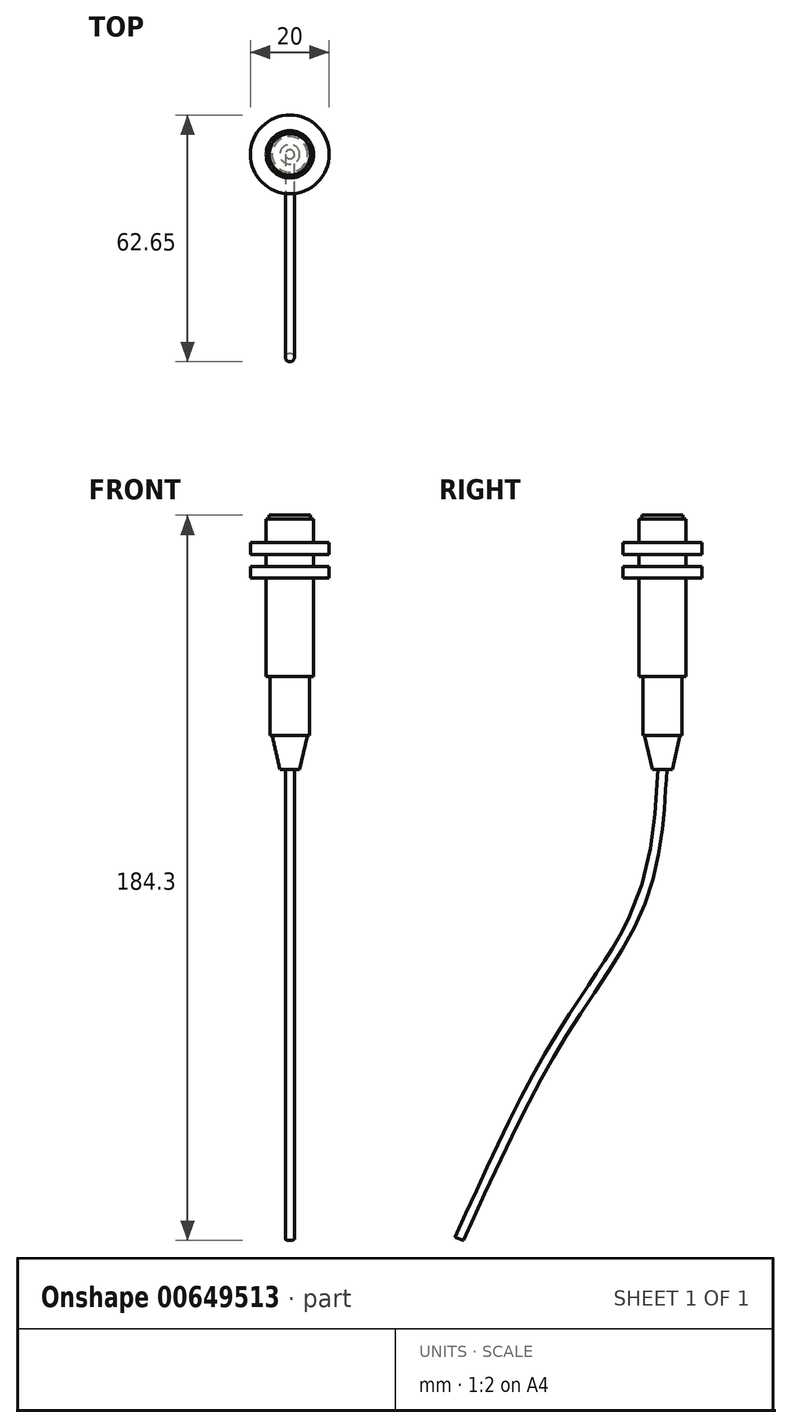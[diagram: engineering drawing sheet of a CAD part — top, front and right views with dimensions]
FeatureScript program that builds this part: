
annotation { "Feature Type Name" : "Feature", "Feature Type Description" : "" }
export const myFeature = defineFeature(function(context is Context, id is Id, definition is map)
    precondition{}
    {
        {
            var Q0;
            Q0=qCreatedBy(makeId("Front.planeOp"),FACE);
            var sketch = newSketch(context, id + "F0", { "sketchPlane" : qUnion([Q0])});
            skLineSegment(sketch, "E0.bottom", {"start": v(0, 0) * mm, "end": v(5, 0) * mm});
            skLineSegment(sketch, "E0.top", {"start": v(0, 15) * mm, "end": v(5, 15) * mm});
            skLineSegment(sketch, "E0.left", {"start": v(0, 0) * mm, "end": v(0, 15) * mm});
            skLineSegment(sketch, "E0.right", {"start": v(5, 0) * mm, "end": v(5, 15) * mm});
            skLineSegment(sketch, "E1.bottom", {"start": v(0, 15) * mm, "end": v(6, 15) * mm});
            skLineSegment(sketch, "E1.top", {"start": v(0, 55) * mm, "end": v(6, 55) * mm});
            skLineSegment(sketch, "E1.left", {"start": v(0, 15) * mm, "end": v(0, 55) * mm});
            skLineSegment(sketch, "E1.right", {"start": v(6, 15) * mm, "end": v(6, 55) * mm});
            skLineSegment(sketch, "E2", {"start": v(0, 0) * mm, "end": v(0, -8.6) * mm});
            skLineSegment(sketch, "E3", {"start": v(0, -8.6) * mm, "end": v(2.52, -8.6) * mm});
            skLineSegment(sketch, "E4", {"start": v(2.52, -8.6) * mm, "end": v(4.5, 0) * mm});
            skLineSegment(sketch, "E5.bottom", {"start": v(0, 55) * mm, "end": v(5.25, 55) * mm});
            skLineSegment(sketch, "E5.top", {"start": v(0, 56) * mm, "end": v(5.25, 56) * mm});
            skLineSegment(sketch, "E5.left", {"start": v(0, 55) * mm, "end": v(0, 56) * mm});
            skLineSegment(sketch, "E5.right", {"start": v(5.25, 55) * mm, "end": v(5.25, 56) * mm});
            skLineSegment(sketch, "E6.bottom", {"start": v(6, 49) * mm, "end": v(10, 49) * mm});
            skLineSegment(sketch, "E6.top", {"start": v(6, 46) * mm, "end": v(10, 46) * mm});
            skLineSegment(sketch, "E6.left", {"start": v(6, 49) * mm, "end": v(6, 46) * mm});
            skLineSegment(sketch, "E6.right", {"start": v(10, 49) * mm, "end": v(10, 46) * mm});
            skLineSegment(sketch, "E7.bottom", {"start": v(6, 43) * mm, "end": v(10, 43) * mm});
            skLineSegment(sketch, "E7.top", {"start": v(6, 40) * mm, "end": v(10, 40) * mm});
            skLineSegment(sketch, "E7.left", {"start": v(6, 43) * mm, "end": v(6, 40) * mm});
            skLineSegment(sketch, "E7.right", {"start": v(10, 43) * mm, "end": v(10, 40) * mm});
            skSolve(sketch);
        }
        {
            var Q0;
            Q0=qSketchRegion(id+"F0",true);
            var Q1;
            Q1=sQuery(id+"F0.wireOp",EDGE,"E1.left");
            revolve(context, id + "F1", {"entities" : qUnion([Q0]), "axis" : qUnion([Q1]), "revolveType" : RevolveType.FULL});
        }
        {
            var Q0;
            Q0=makeQuery(id+"F1.opRevolve","SWEPT_FACE",FACE,{"disambiguationData":[OSD([sQuery(id+"F0.wireOp",EDGE,"E3")])]});
            var sketch = newSketch(context, id + "F2", { "sketchPlane" : qUnion([Q0])});
            skCircle(sketch, "E8", {"center": v(0, 0) * mm, "radius": 1.15 * mm});
            skSolve(sketch);
        }
        {
            var Q0;
            Q0=qCreatedBy(makeId("Right.planeOp"),FACE);
            var sketch = newSketch(context, id + "F3", { "sketchPlane" : qUnion([Q0])});
            skPoint(sketch, "E9.0", {"position": v(0, -8.6) * mm});
            skFitSpline(sketch, "E10", {"points": [v(0, -8.6) * mm, v(-5.45, -42.24) * mm, v(-26.11, -76.88) * mm, v(-51.58, -127.89) * mm], "startDerivative": vector(-6.91, -116.8) * mm, "endDerivative": vector(-63.82, -141.21) * mm});
            skSolve(sketch);
        }
        {
            var Q0;
            Q0=qSketchRegion(id+"F2",true);
            var Q1;
            Q1=qConstructionFilter(qBodyType(qCreatedBy(id+"F3",EDGE),BodyType.WIRE),ConstructionObject.NO);
            sweep(context, id + "F4", {"operationType" : NewBodyOperationType.ADD, "profiles" : qUnion([Q0]), "path" : qUnion([Q1])});
        }
    });
